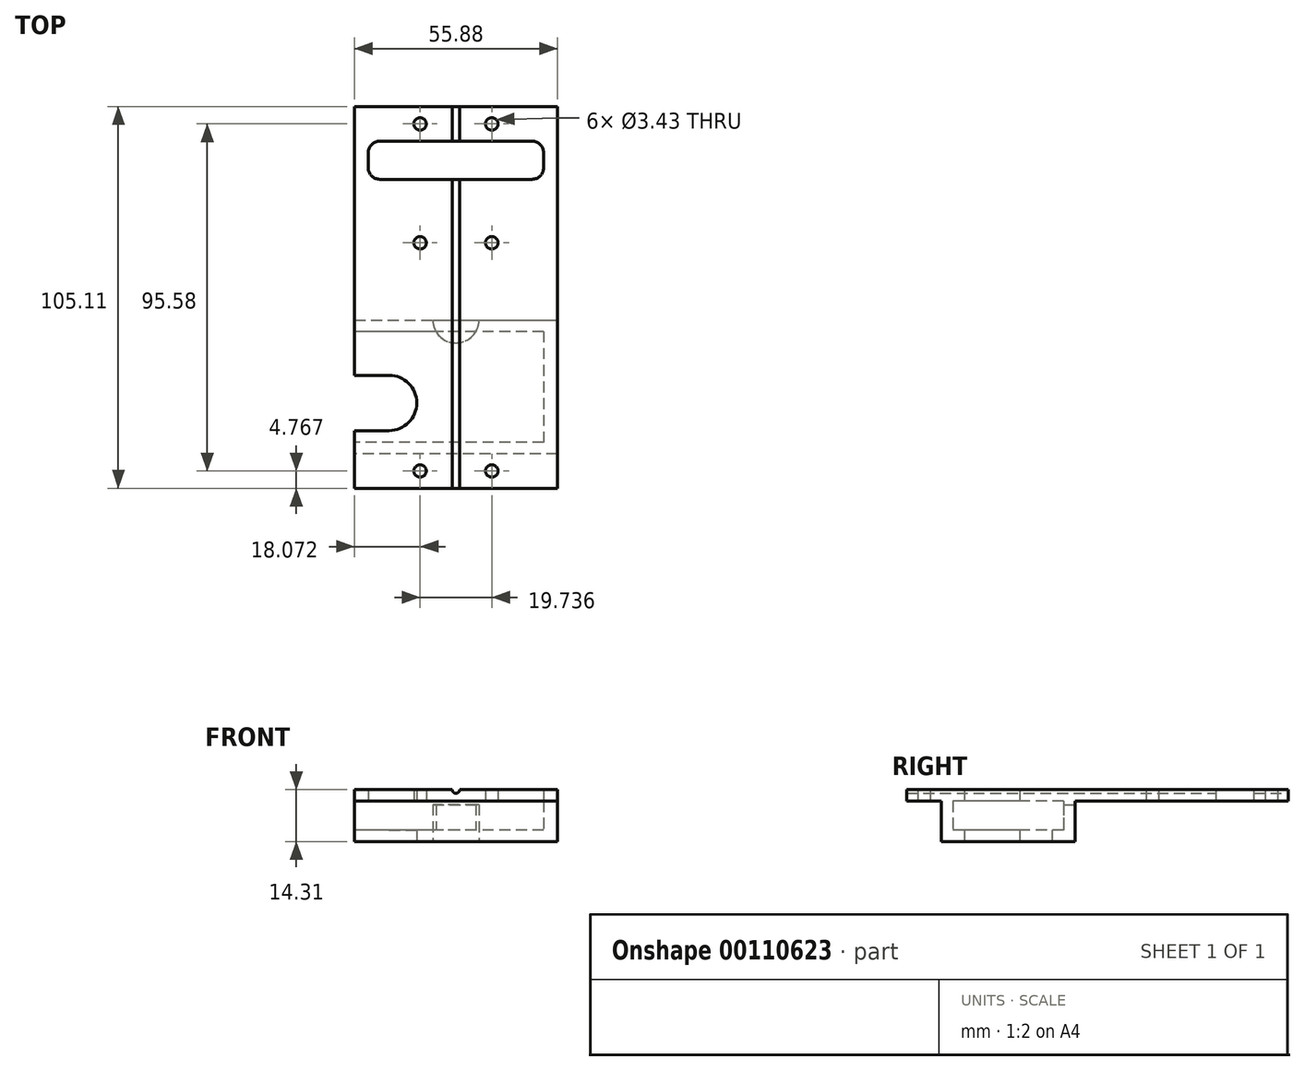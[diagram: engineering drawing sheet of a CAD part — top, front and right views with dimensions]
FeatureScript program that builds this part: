
annotation { "Feature Type Name" : "Feature", "Feature Type Description" : "" }
export const myFeature = defineFeature(function(context is Context, id is Id, definition is map)
    precondition{}
    {
        {
            var Q0;
            Q0=qCreatedBy(makeId("Top.planeOp"),FACE);
            var sketch = newSketch(context, id + "F0", { "sketchPlane" : qUnion([Q0])});
            skLineSegment(sketch, "E0.rect.top", {"start": v(27.94, 0) * mm, "end": v(-27.94, 0) * mm});
            skLineSegment(sketch, "E0.rect.left", {"start": v(27.94, 72.4) * mm, "end": v(27.94, 0) * mm});
            skLineSegment(sketch, "E0.rect.right", {"start": v(-27.94, 72.4) * mm, "end": v(-27.94, 0) * mm});
            skPoint(sketch, "E0.rect.middle", {"position": v(0, 0) * mm});
            skCircle(sketch, "E1", {"center": v(-9.87, 58.09) * mm, "radius": 1.71 * mm});
            skCircle(sketch, "E2", {"center": v(9.87, 58.09) * mm, "radius": 1.71 * mm});
            skLineSegment(sketch, "E3", {"start": v(-12.7, 72.4) * mm, "end": v(12.7, 72.4) * mm, "construction": true});
            skPoint(sketch, "E4", {"position": v(0, 72.4) * mm});
            skLineSegment(sketch, "E5.rect.bottom", {"start": v(24.13, 86.06) * mm, "end": v(-24.13, 86.06) * mm});
            skLineSegment(sketch, "E5.rect.top", {"start": v(24.13, 75.57) * mm, "end": v(-24.13, 75.57) * mm});
            skLineSegment(sketch, "E5.rect.left", {"start": v(24.13, 86.06) * mm, "end": v(24.13, 75.57) * mm});
            skLineSegment(sketch, "E5.rect.right", {"start": v(-24.13, 86.06) * mm, "end": v(-24.13, 75.57) * mm});
            skPoint(sketch, "E5.rect.middle", {"position": v(0, 80.81) * mm});
            skLineSegment(sketch, "E6", {"start": v(-27.94, 72.4) * mm, "end": v(-27.94, 72.4) * mm});
            skLineSegment(sketch, "E7", {"start": v(-27.94, 72.4) * mm, "end": v(-27.94, 95.58) * mm});
            skLineSegment(sketch, "E8", {"start": v(-27.94, 95.58) * mm, "end": v(27.94, 95.58) * mm});
            skLineSegment(sketch, "E9", {"start": v(27.94, 95.58) * mm, "end": v(27.94, 72.4) * mm});
            skLineSegment(sketch, "E10", {"start": v(27.94, 72.4) * mm, "end": v(27.94, 72.4) * mm});
            skPoint(sketch, "E11", {"position": v(0, 95.58) * mm});
            skCircle(sketch, "E12", {"center": v(-9.87, 90.82) * mm, "radius": 1.71 * mm});
            skCircle(sketch, "E13", {"center": v(9.87, 90.82) * mm, "radius": 1.71 * mm});
            skLineSegment(sketch, "E14", {"start": v(0, 86.06) * mm, "end": v(0, 95.58) * mm, "construction": true});
            skPoint(sketch, "E15", {"position": v(0, 90.82) * mm});
            skLineSegment(sketch, "E16", {"start": v(-9.87, 58.09) * mm, "end": v(9.87, 58.09) * mm, "construction": true});
            skPoint(sketch, "E17", {"position": v(0, 58.09) * mm});
            skSolve(sketch);
        }
        {
            var Q0;
            Q0=qSketchRegion(id+"F0",true);
            extrude(context, id + "F1", {"entities" : qUnion([Q0]), "depth" : 3.17 * mm});
        }
        {
            var Q0;
            Q0=makeQuery(id+"F1.opExtrude","CAP_FACE",FACE,{"disambiguationData":[OSD([sQuery(id+"F0.wireOp",EDGE,"E0.rect.bottom"),sQuery(id+"F0.wireOp",EDGE,"E0.rect.top"),sQuery(id+"F0.wireOp",EDGE,"E0.rect.left"),sQuery(id+"F0.wireOp",EDGE,"E0.rect.right")])],"isStart":true});
            var sketch = newSketch(context, id + "F2", { "sketchPlane" : qUnion([Q0])});
            skLineSegment(sketch, "E18.bottom", {"start": v(-27.94, 0) * mm, "end": v(27.94, 0) * mm});
            skLineSegment(sketch, "E18.top", {"start": v(-27.94, -36.83) * mm, "end": v(27.94, -36.83) * mm});
            skLineSegment(sketch, "E18.left", {"start": v(-27.94, 0) * mm, "end": v(-27.94, -36.83) * mm});
            skLineSegment(sketch, "E18.right", {"start": v(27.94, 0) * mm, "end": v(27.94, -36.83) * mm});
            skPoint(sketch, "E19", {"position": v(0, 0) * mm});
            skSolve(sketch);
        }
        {
            var Q0;
            Q0=qSketchRegion(id+"F2",true);
            extrude(context, id + "F3", {"entities" : qUnion([Q0]), "operationType" : NewBodyOperationType.ADD, "depth" : 11.13 * mm});
        }
        {
            var Q0;
            Q0=makeQuery(id+"F3.opExtrude","CAP_FACE",FACE,{"disambiguationData":[OSD([sQuery(id+"F2.wireOp",EDGE,"E18.bottom"),sQuery(id+"F2.wireOp",EDGE,"E18.top"),sQuery(id+"F2.wireOp",EDGE,"E18.left"),sQuery(id+"F2.wireOp",EDGE,"E18.right")])],"isStart":false});
            var sketch = newSketch(context, id + "F4", { "sketchPlane" : qUnion([Q0])});
            skLineSegment(sketch, "E20", {"start": v(-27.94, -21.59) * mm, "end": v(-27.94, -6.35) * mm});
            skLineSegment(sketch, "E21", {"start": v(-27.94, -6.35) * mm, "end": v(-18.42, -6.35) * mm});
            skLineSegment(sketch, "E22", {"start": v(-27.94, -21.59) * mm, "end": v(-18.42, -21.59) * mm});
            skArc(sketch, "E23", {"start": v(-18.42, -21.59) * mm, "mid": v(-10.8, -13.97) * mm, "end": v(-18.42, -6.35) * mm});
            skSolve(sketch);
        }
        {
            var Q0;
            Q0=qSketchRegion(id+"F4",true);
            extrude(context, id + "F5", {"entities" : qUnion([Q0]), "operationType" : NewBodyOperationType.REMOVE, "endBound" : BoundingType.THROUGH_ALL, "oppositeDirection" : true, "depth" : 25.4 * mm});
        }
        {
            var Q0;
            Q0=makeQuery(id+"F3.boolean.opBoolean","MERGE",FACE,{"derivedFrom":[makeQuery(id+"F1.opExtrude","SWEPT_FACE",FACE,{"disambiguationData":[OSD([sQuery(id+"F0.wireOp",EDGE,"E0.rect.top")])]}),makeQuery(id+"F3.opExtrude","SWEPT_FACE",FACE,{"disambiguationData":[OSD([sQuery(id+"F2.wireOp",EDGE,"E18.bottom")])]})]});
            var sketch = newSketch(context, id + "F6", { "sketchPlane" : qUnion([Q0])});
            skLineSegment(sketch, "E24.bottom", {"start": v(-27.94, 3.18) * mm, "end": v(27.94, 3.18) * mm});
            skLineSegment(sketch, "E24.top", {"start": v(-27.94, 0) * mm, "end": v(27.94, 0) * mm});
            skLineSegment(sketch, "E24.left", {"start": v(-27.94, 3.18) * mm, "end": v(-27.94, 0) * mm});
            skLineSegment(sketch, "E24.right", {"start": v(27.94, 3.18) * mm, "end": v(27.94, 0) * mm});
            skSolve(sketch);
        }
        {
            var Q0;
            Q0 = qSketchRegion(id + "F6", true);
            extrude(context, id + "F7", {"entities" : qUnion([Q0]), "operationType" : NewBodyOperationType.ADD, "depth" : 9.52 * mm});
        }
        {
            var Q0;
            Q0=makeQuery(id+"F1.opExtrude","SWEPT_FACE",FACE,{"disambiguationData":[OSD([sQuery(id+"F0.wireOp",EDGE,"E8")])]});
            var sketch = newSketch(context, id + "F8", { "sketchPlane" : qUnion([Q0])});
            skCircle(sketch, "E25", {"center": v(0, 3.18) * mm, "radius": 1.02 * mm});
            skSolve(sketch);
        }
        {
            var Q0;
            Q0=qSketchRegion(id+"F8",true);
            extrude(context, id + "F9", {"entities" : qUnion([Q0]), "operationType" : NewBodyOperationType.REMOVE, "endBound" : BoundingType.THROUGH_ALL, "oppositeDirection" : true, "depth" : 25.4 * mm});
        }
        {
            var Q0;
            {var subQ0=sQuery(id+"F0.wireOp",EDGE,"E8");var subQ4=sQuery(id+"F0.wireOp",EDGE,"E7");var subQ11=sQuery(id+"F0.wireOp",EDGE,"E0.rect.right");var subQ14=sQuery(id+"F2.wireOp",EDGE,"E18.left");Q0=makeQuery(id+"F5.boolean.opBoolean","SPLIT",FACE,{"disambiguationData":[TD([makeQuery(id+"F1.opExtrude","SWEPT_FACE",FACE,{"disambiguationData":[OSD([subQ0])]})])],"derivedFrom":makeQuery(id+"F3.boolean.opBoolean","MERGE",FACE,{"derivedFrom":[makeQuery(id+"F1.opExtrude","SWEPT_FACE",FACE,{"disambiguationData":[OSD([subQ11,subQ4])]}),makeQuery(id+"F3.opExtrude","SWEPT_FACE",FACE,{"disambiguationData":[OSD([subQ14])]})]})});}
            var sketch = newSketch(context, id + "F10", { "sketchPlane" : qUnion([Q0])});
            skLineSegment(sketch, "E26.bottom", {"start": v(-33.66, 0) * mm, "end": v(-3.18, 0) * mm});
            skLineSegment(sketch, "E26.top", {"start": v(-33.66, -7.95) * mm, "end": v(-3.18, -7.95) * mm});
            skLineSegment(sketch, "E26.left", {"start": v(-33.66, 0) * mm, "end": v(-33.66, -7.95) * mm});
            skLineSegment(sketch, "E26.right", {"start": v(-3.18, 0) * mm, "end": v(-3.18, -7.95) * mm});
            skSolve(sketch);
        }
        {
            var Q0;
            Q0=qSketchRegion(id+"F10",true);
            extrude(context, id + "F11", {"entities" : qUnion([Q0]), "operationType" : NewBodyOperationType.REMOVE, "oppositeDirection" : true, "depth" : 52.07 * mm});
        }
        {
            var Q0;
            Q0=makeQuery(id+"F1.opExtrude","SWEPT_EDGE",EDGE,{"disambiguationData":[OSD([sQuery(id+"F0.wireOp",EDGE,"E5.rect.top"),sQuery(id+"F0.wireOp",EDGE,"E5.rect.left")])]});
            var Q1;
            Q1=makeQuery(id+"F1.opExtrude","SWEPT_EDGE",EDGE,{"disambiguationData":[OSD([sQuery(id+"F0.wireOp",EDGE,"E5.rect.top"),sQuery(id+"F0.wireOp",EDGE,"E5.rect.right")])]});
            var Q2;
            Q2=makeQuery(id+"F1.opExtrude","SWEPT_EDGE",EDGE,{"disambiguationData":[OSD([sQuery(id+"F0.wireOp",EDGE,"E5.rect.bottom"),sQuery(id+"F0.wireOp",EDGE,"E5.rect.right")])]});
            var Q3;
            Q3=makeQuery(id+"F1.opExtrude","SWEPT_EDGE",EDGE,{"disambiguationData":[OSD([sQuery(id+"F0.wireOp",EDGE,"E5.rect.bottom"),sQuery(id+"F0.wireOp",EDGE,"E5.rect.left")])]});
            fillet(context, id + "F12", {"entities" : qUnion([Q0, Q1, Q2, Q3]), "radius" : 3.17 * mm, "tangentPropagation" : true, "allowEdgeOverflow" : false});
        }
        {
            var Q0;
            Q0=makeQuery(id+"F7.opExtrude","SWEPT_FACE",FACE,{"disambiguationData":[OSD([sQuery(id+"F6.wireOp",EDGE,"E24.top")])]});
            var sketch = newSketch(context, id + "F13", { "sketchPlane" : qUnion([Q0])});
            skCircle(sketch, "E27", {"center": v(-9.87, 4.76) * mm, "radius": 1.71 * mm});
            skCircle(sketch, "E28", {"center": v(9.87, 4.76) * mm, "radius": 1.71 * mm});
            skCircle(sketch, "E29", {"center": v(-9.87, -58.09) * mm, "radius": 1.71 * mm, "construction": true});
            skCircle(sketch, "E30", {"center": v(9.87, -58.09) * mm, "radius": 1.71 * mm, "construction": true});
            skLineSegment(sketch, "E31", {"start": v(-9.87, 9.52) * mm, "end": v(-9.87, 0) * mm, "construction": true});
            skSolve(sketch);
        }
        {
            var Q0;
            Q0 = qSketchRegion(id + "F13", true);
            extrude(context, id + "F14", {"entities" : qUnion([Q0]), "operationType" : NewBodyOperationType.REMOVE, "oppositeDirection" : true, "depth" : 25.4 * mm});
        }
        {
            var Q0;
            Q0=makeQuery(id+"F3.opExtrude","CAP_FACE",FACE,{"disambiguationData":[OSD([sQuery(id+"F2.wireOp",EDGE,"E18.bottom"),sQuery(id+"F2.wireOp",EDGE,"E18.top"),sQuery(id+"F2.wireOp",EDGE,"E18.left"),sQuery(id+"F2.wireOp",EDGE,"E18.right")])],"isStart":false});
            var sketch = newSketch(context, id + "F15", { "sketchPlane" : qUnion([Q0])});
            skArc(sketch, "E32", {"start": v(6.35, -36.83) * mm, "mid": v(0, -30.48) * mm, "end": v(-6.35, -36.83) * mm});
            skLineSegment(sketch, "E33", {"start": v(-6.35, -36.83) * mm, "end": v(6.35, -36.83) * mm});
            skSolve(sketch);
        }
        {
            var Q0;
            Q0 = qSketchRegion(id + "F15", true);
            extrude(context, id + "F16", {"entities" : qUnion([Q0]), "operationType" : NewBodyOperationType.REMOVE, "oppositeDirection" : true, "depth" : 10.16 * mm});
        }
    });
